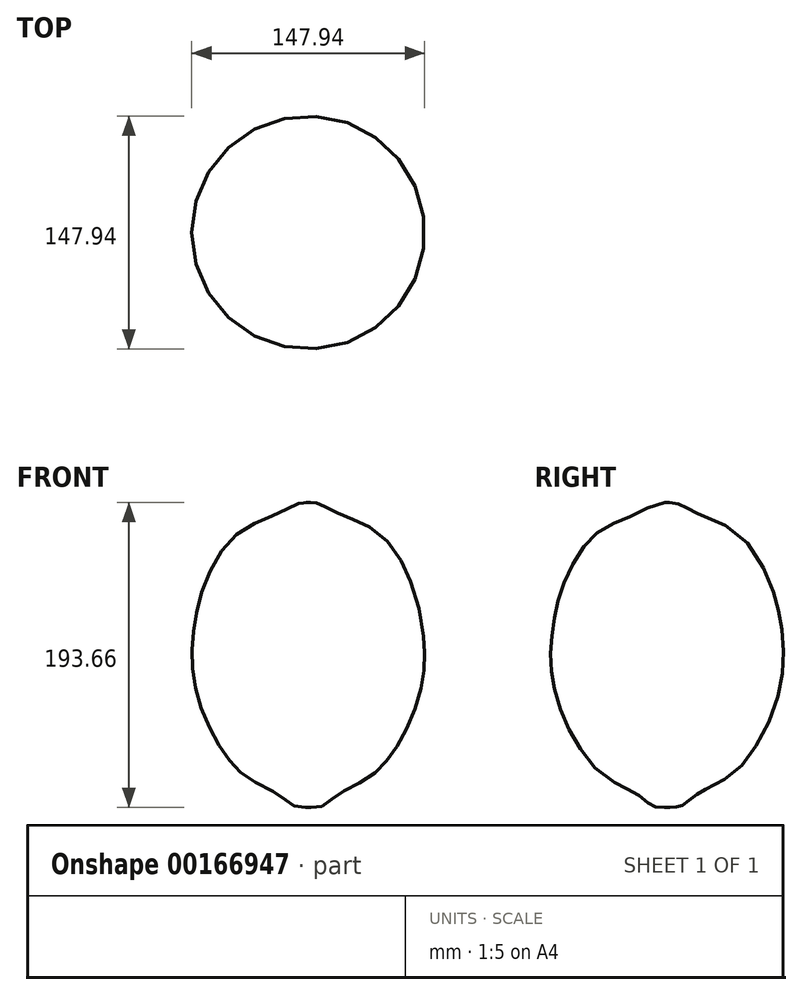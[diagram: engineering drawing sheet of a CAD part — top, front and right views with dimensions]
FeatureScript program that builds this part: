
annotation { "Feature Type Name" : "Feature", "Feature Type Description" : "" }
export const myFeature = defineFeature(function(context is Context, id is Id, definition is map)
    precondition{}
    {
        {
            var Q0;
            Q0=qCreatedBy(makeId("Front.planeOp"),FACE);
            var sketch = newSketch(context, id + "F0", { "sketchPlane" : qUnion([Q0])});
            skLineSegment(sketch, "E0", {"start": v(0, 94.23) * mm, "end": v(0, -99.36) * mm});
            skFitSpline(sketch, "E1", {"points": [v(0, -99.36) * mm, v(-9.5, -98.27) * mm, v(-17.11, -92.4) * mm, v(-38.58, -80.34) * mm, v(-52.55, -66.13) * mm, v(-66.53, -40.4) * mm, v(-73.57, -11.17) * mm, v(-72.87, 13.26) * mm, v(-65.82, 42.26) * mm, v(-45.5, 74.09) * mm, v(-20.6, 86.65) * mm, v(-7.13, 93.28) * mm, v(0, 94.23) * mm], "startDerivative": vector(-184.3, -1.76) * mm, "endDerivative": vector(154.76, -10.32) * mm});
            skSolve(sketch);
        }
        {
            var Q0;
            Q0=makeQuery(id+"F0.imprint","IMPRINT",FACE,{"disambiguationData":[TD([[makeQuery(id+"F0.imprint","IMPRINT",EDGE,{"derivedFrom":sQuery(id+"F0.wireOp",EDGE,"E0")}),-1.0]])]});
            var Q1;
            Q1=sQuery(id+"F0.wireOp",EDGE,"E0");
            revolve(context, id + "F1", {"entities" : qUnion([Q0]), "axis" : qUnion([Q1]), "revolveType" : RevolveType.FULL});
        }
    });
